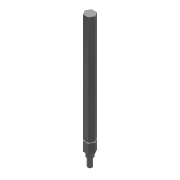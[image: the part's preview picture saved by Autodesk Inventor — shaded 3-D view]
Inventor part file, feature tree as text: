
AUTODESK INVENTOR PART (.ipt)
format: ipt  version: 2015 (Build 190159000, 159)  size: 107,520 bytes
history: native  units: in
note: dims shown in document units (in); Inventor stores cm internally (conversion verified against a paired STEP export)
features: chamfer x1, other x1, extrude x1, imported_body x1, sketch x1
ambient origin geometry x8: Origin, YZ Plane, XZ Plane, XY Plane, X Axis, Y Axis, Z Axis, Center Point
bodies: Body1 (feature_tree)
feature tree (5):
  chamfer  "Chamfer1"  Distance=3.556in
  other  "TB Output Shaft AM14U1"
  extrude  "Extrusion1"  [1 undecoded]
  imported_body  "Base1"
  sketch  "Sketch1"
note: 1 required parameter value undecoded (feature->parameter linkage not recoverable at this tier; creation-order binding heuristic only, values carry confidence <= 0.55)
